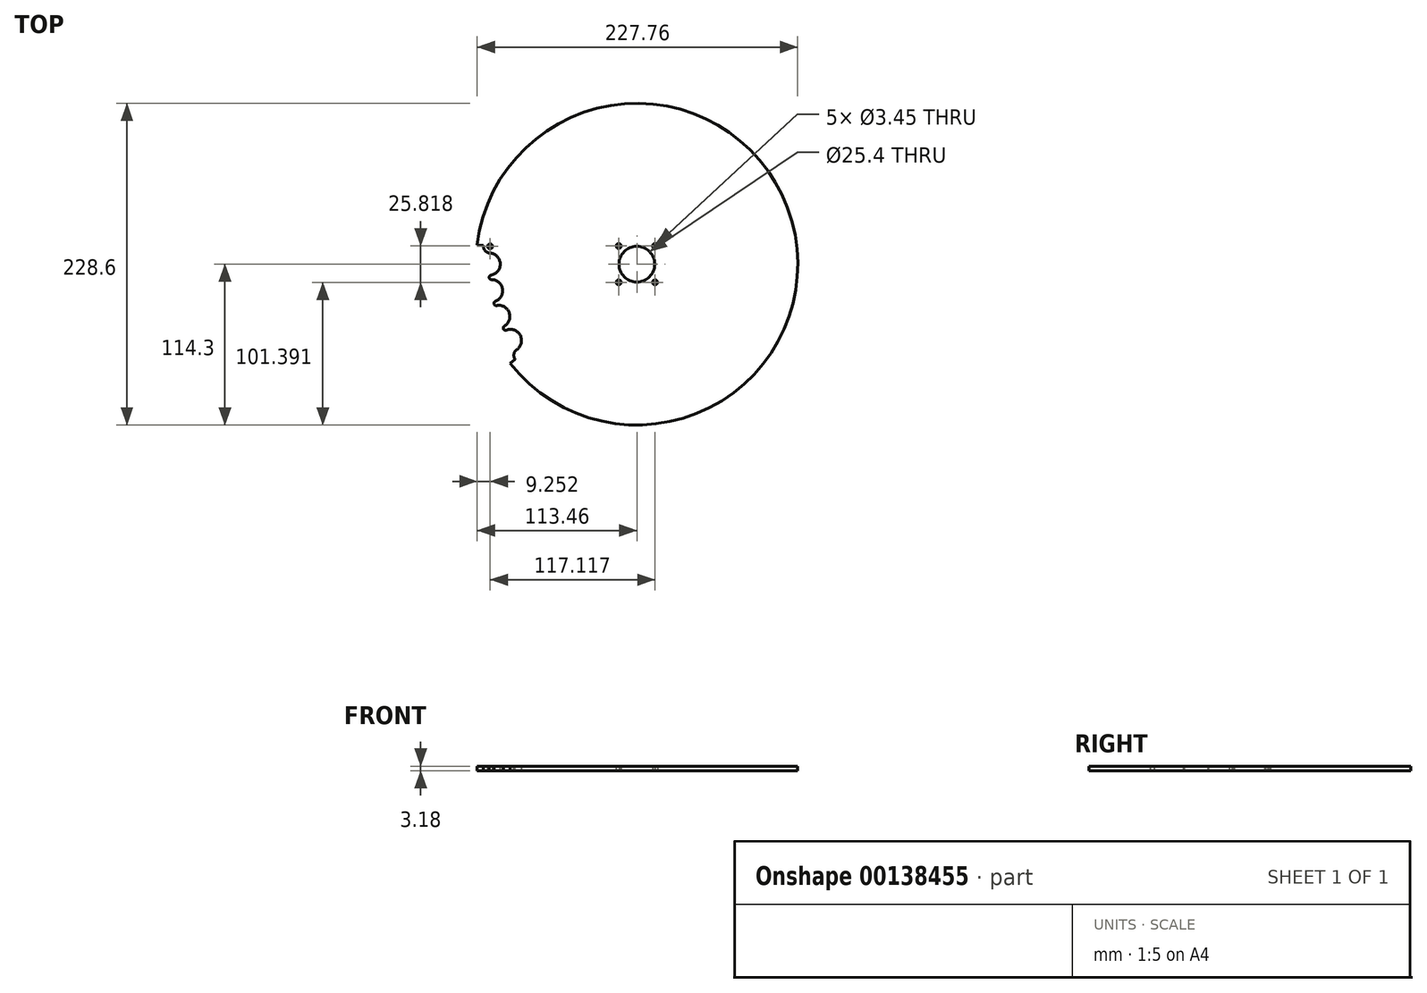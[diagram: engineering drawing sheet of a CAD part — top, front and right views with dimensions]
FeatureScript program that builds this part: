
annotation { "Feature Type Name" : "Feature", "Feature Type Description" : "" }
export const myFeature = defineFeature(function(context is Context, id is Id, definition is map)
    precondition{}
    {
        {
            var Q0;
            Q0=qCreatedBy(makeId("Top.planeOp"),FACE);
            var sketch = newSketch(context, id + "F0", { "sketchPlane" : qUnion([Q0])});
            skCircle(sketch, "E0", {"center": v(0, 0) * mm, "radius": 114.3 * mm});
            skCircle(sketch, "E1", {"center": v(0, 0) * mm, "radius": 12.7 * mm});
            skCircle(sketch, "E2", {"center": v(0, 0) * mm, "radius": 14.29 * mm, "construction": true});
            skLineSegment(sketch, "E3.bottom", {"start": v(-12.9, -12.9) * mm, "end": v(12.9, -12.9) * mm, "construction": true});
            skLineSegment(sketch, "E3.top", {"start": v(-12.9, 12.9) * mm, "end": v(12.9, 12.9) * mm, "construction": true});
            skLineSegment(sketch, "E3.left", {"start": v(-12.9, -12.9) * mm, "end": v(-12.9, 12.9) * mm, "construction": true});
            skLineSegment(sketch, "E3.right", {"start": v(12.9, -12.9) * mm, "end": v(12.9, 12.9) * mm, "construction": true});
            skCircle(sketch, "E4", {"center": v(-12.9, -12.9) * mm, "radius": 3.97 * mm, "construction": true});
            skCircle(sketch, "E5", {"center": v(-12.9, -12.9) * mm, "radius": 1.73 * mm});
            skCircle(sketch, "E6", {"center": v(-12.9, 12.9) * mm, "radius": 1.73 * mm});
            skCircle(sketch, "E7", {"center": v(12.9, 12.9) * mm, "radius": 1.73 * mm});
            skCircle(sketch, "E8", {"center": v(12.9, -12.9) * mm, "radius": 1.73 * mm});
            skSolve(sketch);
        }
        {
            var Q0;
            Q0=qSketchRegion(id+"F0",true);
            extrude(context, id + "F1", {"entities" : qUnion([Q0]), "depth" : 3.17 * mm});
        }
        {
            var Q0;
            Q0=makeQuery(id+"F1.opExtrude","CAP_FACE",FACE,{"disambiguationData":[OSD([sQuery(id+"F0.wireOp",EDGE,"E0"),sQuery(id+"F0.wireOp",EDGE,"E1")])],"isStart":false});
            var sketch = newSketch(context, id + "F2", { "sketchPlane" : qUnion([Q0])});
            skLineSegment(sketch, "E9", {"start": v(0, 0) * mm, "end": v(-104.98, 0) * mm, "construction": true});
            skLineSegment(sketch, "E10", {"start": v(-104.98, 0) * mm, "end": v(-114.3, 0) * mm, "construction": true});
            skCircle(sketch, "E11", {"center": v(-104.98, 0) * mm, "radius": 6.15 * mm, "construction": true});
            skLineSegment(sketch, "E12", {"start": v(0, 0) * mm, "end": v(-103.26, -18.9) * mm, "construction": true});
            skLineSegment(sketch, "E13", {"start": v(0, 0) * mm, "end": v(-98.17, -37.2) * mm, "construction": true});
            skLineSegment(sketch, "E14", {"start": v(0, 0) * mm, "end": v(-89.86, -54.27) * mm, "construction": true});
            skLineSegment(sketch, "E15", {"start": v(0, 0) * mm, "end": v(-104.2, 12.68) * mm, "construction": true});
            skCircle(sketch, "E16", {"center": v(-103.26, -18.9) * mm, "radius": 6.15 * mm, "construction": true});
            skCircle(sketch, "E17", {"center": v(-98.17, -37.2) * mm, "radius": 6.15 * mm, "construction": true});
            skCircle(sketch, "E18", {"center": v(-89.86, -54.27) * mm, "radius": 6.15 * mm, "construction": true});
            skLineSegment(sketch, "E19", {"start": v(-104.98, 0) * mm, "end": v(-103.26, -18.9) * mm, "construction": true});
            skLineSegment(sketch, "E20", {"start": v(-98.17, -37.2) * mm, "end": v(-103.26, -18.9) * mm, "construction": true});
            skLineSegment(sketch, "E21", {"start": v(-98.17, -37.2) * mm, "end": v(-89.86, -54.27) * mm, "construction": true});
            skCircle(sketch, "E22", {"center": v(-104.2, 12.68) * mm, "radius": 1.73 * mm});
            skLineSegment(sketch, "E23", {"start": v(-104.2, 12.68) * mm, "end": v(-104.98, 0) * mm, "construction": true});
            skLineSegment(sketch, "E24", {"start": v(0, 0) * mm, "end": v(-82.65, -64.72) * mm, "construction": true});
            skLineSegment(sketch, "E25", {"start": v(-82.65, -64.72) * mm, "end": v(-89.86, -54.27) * mm, "construction": true});
            skCircle(sketch, "E26", {"center": v(-104.2, 12.68) * mm, "radius": 6.35 * mm, "construction": true});
            skCircle(sketch, "E27", {"center": v(-104.98, 0) * mm, "radius": 6.35 * mm, "construction": true});
            skSolve(sketch);
        }
        {
            var Q0;
            Q0=qSketchRegion(id+"F2",true);
            var Q1;
            Q1=makeQuery(id+"F1.opExtrude","CAP_FACE",FACE,{"disambiguationData":[OSD([sQuery(id+"F0.wireOp",EDGE,"E0"),sQuery(id+"F0.wireOp",EDGE,"E1")])],"isStart":true});
            extrude(context, id + "F3", {"entities" : qUnion([Q0]), "operationType" : NewBodyOperationType.REMOVE, "endBound" : BoundingType.UP_TO_SURFACE, "oppositeDirection" : true, "endBoundEntityFace" : qUnion([Q1]), "depth" : 25.4 * mm});
        }
        {
            var Q0;
            Q0=makeQuery(id+"F2.imprint","IMPRINT",FACE,{"disambiguationData":[TD([[makeQuery(id+"F2.imprint","IMPRINT",EDGE,{"derivedFrom":sQuery(id+"F2.wireOp",EDGE,"E22")}),-1.0]])]});
            var sketch = newSketch(context, id + "F4", { "sketchPlane" : qUnion([Q0])});
            skArc(sketch, "E28", {"start": v(-85.35, -60.8) * mm, "mid": v(-87.36, -64) * mm, "end": v(-86.4, -67.66) * mm});
            skArc(sketch, "E29", {"start": v(-85.35, -60.8) * mm, "mid": v(-82.85, -50.55) * mm, "end": v(-92.73, -46.87) * mm});
            skArc(sketch, "E30", {"start": v(-94.12, -44.02) * mm, "mid": v(-94.73, -46.08) * mm, "end": v(-92.73, -46.87) * mm});
            skArc(sketch, "E31", {"start": v(-94.12, -44.02) * mm, "mid": v(-90.74, -34.38) * mm, "end": v(-99.66, -29.4) * mm});
            skLineSegment(sketch, "E32", {"start": v(-86.4, -67.66) * mm, "end": v(-90, -70.47) * mm});
            skLineSegment(sketch, "E33", {"start": v(-82.65, -64.72) * mm, "end": v(-86.4, -67.66) * mm, "construction": true});
            skArc(sketch, "E34", {"start": v(-108.94, 13.25) * mm, "mid": v(-107.87, 9.63) * mm, "end": v(-104.5, 7.92) * mm});
            skArc(sketch, "E35", {"start": v(-100.5, -26.35) * mm, "mid": v(-95.45, -17.48) * mm, "end": v(-103.32, -10.97) * mm});
            skArc(sketch, "E36", {"start": v(-103.6, -7.82) * mm, "mid": v(-97.05, 0.45) * mm, "end": v(-104.5, 7.92) * mm});
            skArc(sketch, "E37", {"start": v(-103.6, -7.82) * mm, "mid": v(-104.92, -9.53) * mm, "end": v(-103.32, -10.97) * mm});
            skArc(sketch, "E38", {"start": v(-100.5, -26.35) * mm, "mid": v(-101.48, -28.27) * mm, "end": v(-99.66, -29.4) * mm});
            skLineSegment(sketch, "E39", {"start": v(-104.2, 12.68) * mm, "end": v(-108.94, 13.25) * mm, "construction": true});
            skLineSegment(sketch, "E40", {"start": v(-108.94, 13.25) * mm, "end": v(-113.46, 13.8) * mm});
            skArc(sketch, "E41", {"start": v(-113.46, 13.8) * mm, "mid": v(-110.1, -30.67) * mm, "end": v(-90, -70.47) * mm});
            skSolve(sketch);
        }
        {
            var Q0;
            Q0 = qSketchRegion(id + "F4", true);
            var Q1;
            Q1=makeQuery(id+"F1.opExtrude","CAP_FACE",FACE,{"disambiguationData":[OSD([sQuery(id+"F0.wireOp",EDGE,"E0"),sQuery(id+"F0.wireOp",EDGE,"E1"),sQuery(id+"F0.wireOp",EDGE,"E5"),sQuery(id+"F0.wireOp",EDGE,"E6"),sQuery(id+"F0.wireOp",EDGE,"E7"),sQuery(id+"F0.wireOp",EDGE,"E8")])],"isStart":true});
            extrude(context, id + "F5", {"entities" : qUnion([Q0]), "operationType" : NewBodyOperationType.REMOVE, "endBound" : BoundingType.UP_TO_SURFACE, "oppositeDirection" : true, "endBoundEntityFace" : qUnion([Q1]), "depth" : 25.4 * mm});
        }
    });
